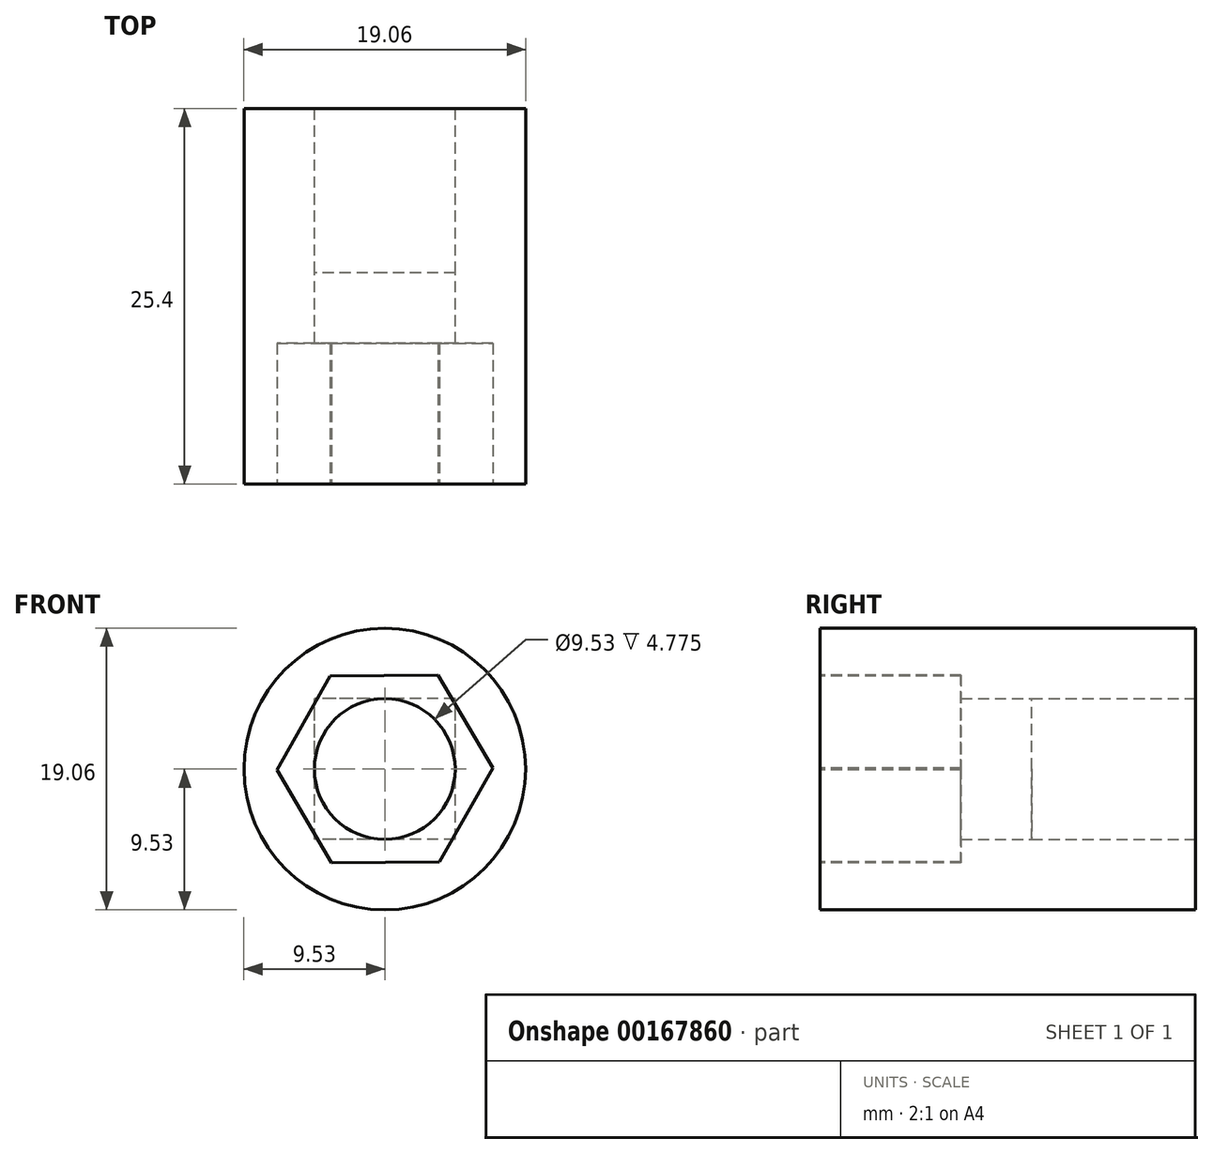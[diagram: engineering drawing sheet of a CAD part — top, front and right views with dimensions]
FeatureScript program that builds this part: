
annotation { "Feature Type Name" : "Feature", "Feature Type Description" : "" }
export const myFeature = defineFeature(function(context is Context, id is Id, definition is map)
    precondition{}
    {
        {
            var Q0;
            Q0=qCreatedBy(makeId("Front.planeOp"),FACE);
            var sketch = newSketch(context, id + "F0", { "sketchPlane" : qUnion([Q0])});
            skCircle(sketch, "E0", {"center": v(0, 0) * mm, "radius": 9.53 * mm});
            skSolve(sketch);
        }
        {
            var Q0;
            Q0=makeQuery(id+"F0.imprint","IMPRINT",FACE,{"disambiguationData":[TD([[makeQuery(id+"F0.imprint","IMPRINT",EDGE,{"derivedFrom":sQuery(id+"F0.wireOp",EDGE,"E0")}),1.0]])]});
            extrude(context, id + "F1", {"entities" : qUnion([Q0]), "depth" : 25.4 * mm});
        }
        {
            var Q0;
            Q0=qCreatedBy(makeId("Front.planeOp"),FACE);
            var sketch = newSketch(context, id + "F2", { "sketchPlane" : qUnion([Q0])});
            skLineSegment(sketch, "E1.bottom", {"start": v(4.76, -4.76) * mm, "end": v(-4.76, -4.76) * mm});
            skLineSegment(sketch, "E1.top", {"start": v(4.76, 4.76) * mm, "end": v(-4.76, 4.76) * mm});
            skLineSegment(sketch, "E1.left", {"start": v(4.76, -4.76) * mm, "end": v(4.76, 4.76) * mm});
            skLineSegment(sketch, "E1.right", {"start": v(-4.76, -4.76) * mm, "end": v(-4.76, 4.76) * mm});
            skPoint(sketch, "E1.middle", {"position": v(0, 0) * mm});
            skCircle(sketch, "E2", {"center": v(0, 0) * mm, "radius": 4.76 * mm});
            skSolve(sketch);
        }
        {
            var Q0;
            {var subQ0=sQuery(id+"F2.wireOp",EDGE,"E2");var subQ1=makeQuery(id+"F2.imprint","INTERSECT",VERTEX,{"derivedFrom":[sQuery(id+"F2.wireOp",EDGE,"E1.top"),subQ0]});Q0=makeQuery(id+"F2.imprint","IMPRINT",FACE,{"disambiguationData":[TD([[makeQuery(id+"F2.imprint","IMPRINT",EDGE,{"disambiguationData":[TD([[subQ1,1.0]])],"derivedFrom":subQ0}),1.0]])]});}
            extrude(context, id + "F3", {"entities" : qUnion([Q0]), "operationType" : NewBodyOperationType.REMOVE, "endBound" : BoundingType.THROUGH_ALL, "depth" : 25.4 * mm});
        }
        {
            var Q0;
            Q0 = qSketchRegion(id + "F2", true);
            extrude(context, id + "F4", {"entities" : qUnion([Q0]), "operationType" : NewBodyOperationType.REMOVE, "depth" : 11.1 * mm});
        }
        {
            var Q0;
            Q0=makeQuery(id+"F1.opExtrude","CAP_FACE",FACE,{"disambiguationData":[OSD([sQuery(id+"F0.wireOp",EDGE,"E0")])],"isStart":false});
            var sketch = newSketch(context, id + "F5", { "sketchPlane" : qUnion([Q0])});
            skCircle(sketch, "E3.cCircle", {"center": v(0, 0) * mm, "radius": 6.32 * mm, "construction": true});
            skLineSegment(sketch, "E3.0", {"start": v(3.6, 6.36) * mm, "end": v(7.3, 0.06) * mm});
            skLineSegment(sketch, "E3.1", {"start": v(7.3, 0.06) * mm, "end": v(3.7, -6.3) * mm});
            skLineSegment(sketch, "E3.2", {"start": v(3.7, -6.3) * mm, "end": v(-3.6, -6.36) * mm});
            skLineSegment(sketch, "E3.3", {"start": v(-3.6, -6.36) * mm, "end": v(-7.3, -0.06) * mm});
            skLineSegment(sketch, "E3.4", {"start": v(-7.3, -0.06) * mm, "end": v(-3.7, 6.3) * mm});
            skLineSegment(sketch, "E3.5", {"start": v(-3.7, 6.3) * mm, "end": v(3.6, 6.36) * mm});
            skPoint(sketch, "E3.0.midPoint", {"position": v(5.45, 3.21) * mm});
            skSolve(sketch);
        }
        {
            var Q0;
            Q0 = qSketchRegion(id + "F5", true);
            extrude(context, id + "F6", {"entities" : qUnion([Q0]), "operationType" : NewBodyOperationType.REMOVE, "oppositeDirection" : true, "depth" : 9.52 * mm});
        }
    });
